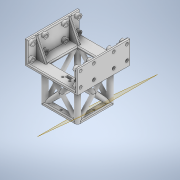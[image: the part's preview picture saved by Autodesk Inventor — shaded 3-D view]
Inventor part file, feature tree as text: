
AUTODESK INVENTOR PART (.ipt)
format: ipt  version: 2022 (Build 260153000, 153)  size: 548,352 bytes
history: native  units: in
note: dims shown in document units (in); Inventor stores cm internally (conversion verified against a paired STEP export)
features: extrude x14, sketch x14, mirror x5, pattern_circular x2, plane x1, fillet x1
ambient origin geometry x8: Origin, YZ Plane, XZ Plane, XY Plane, X Axis, Y Axis, Z Axis, Center Point
bodies: Solid1 (feature_tree)
feature tree (37):
  extrude  "Extrusion1"  Depth=4.0551in
  extrude  "Extrusion2"  Depth=0.1969in
  extrude  "Extrusion3"  Depth=1.5748in TaperAngle=0.0deg
  extrude  "Extrusion4"  Depth=0.3937in
  mirror  "Mirror1"
  extrude  "Extrusion5"  Depth=0.3937in
  extrude  "Extrusion6"  Depth=0.3937in
  extrude  "Extrusion7"  Depth=0.3937in
  extrude  "Extrusion8"  Depth=0.2362in
  pattern_circular  "Circular Pattern1"  [2 undecoded]
  plane  "Work Plane1"
  extrude  "Extrusion9"  Depth=0.0787in
  mirror  "Mirror2"
  pattern_circular  "Circular Pattern2"  [2 undecoded]
  extrude  "Extrusion10"  Depth=0.0787in
  extrude  "Extrusion11"  Depth=0.0787in
  mirror  "Mirror3"
  extrude  "Extrusion12"  Depth=0.0787in
  extrude  "Extrusion13"  Depth=0.0787in
  mirror  "Mirror4"
  mirror  "Mirror5"
  extrude  "Extrusion14"  Depth=0.0787in
  fillet  "Fillet1"  Radius=0.2362in
  sketch  "Sketch1"  dims[d0=4.0551in d1=4.0551in]
  sketch  "Sketch2"  dims[d2=0.1969in d3=0.0in d4=0.1969in]
  sketch  "Sketch3"  dims[d5=0.1969in d6=1.5748in d7=0.0in]
  sketch  "Sketch4"  dims[d8=0.3937in d9=0.3937in]
  sketch  "Sketch5"  dims[d10=0.3937in d11=0.3937in]
  sketch  "Sketch6"  dims[d12=0.3937in d13=0.3937in]
  sketch  "Sketch7"  dims[d14=0.3937in d15=0.3937in]
  sketch  "Sketch8"  dims[d16=0.2362in d17=0.2362in]
  sketch  "Sketch9"  dims[d18=0.2362in]
  sketch  "Sketch10"  dims[d19=0.2362in]
  sketch  "Sketch11"  dims[d20=0.2362in]
  sketch  "Sketch12"  dims[d21=0.2362in]
  sketch  "Sketch13"  dims[d22=0.2362in]
  sketch  "Sketch14"  dims[d23=0.2362in d24=0.1969in d25=0.0in d26=0.2362in d27=0.2362in d28=0.2362in d29=0.2362in d30=0.2362in d31=0.2362in d32=0.2362in d33=0.2362in d34=0.7874in d35=0.0in d36=0.3937in d37=0.3937in d38=0.3937in d39=0.3937in d40=2.5591in d41=0.0in d42=0.1969in d43=0.0in d44=2.126in d45=2.126in d46=3.937in d47=0.0in d48=0.1575in d49=0.2362in d50=0.0in d51=1.5748in d52=360.0deg d54=0.2886in d55=0.2953in d56=3.2677in d57=0.0in d58=0.0787in d59=0.0in d60=1.5748in d61=360.0deg d63=0.1969in d64=0.1969in d65=0.1969in d66=0.1969in d67=0.2362in d68=0.0in d69=0.1575in d70=0.1575in d71=0.2362in d72=0.0in d73=0.1969in d74=0.1969in d75=0.1969in d76=1.5748in d77=0.0in d78=0.2362in d79=0.0in d80=5.9055in d81=0.0in d82=0.0787in]
note: 4 required parameter values undecoded (feature->parameter linkage not recoverable at this tier; creation-order binding heuristic only, values carry confidence <= 0.55)
